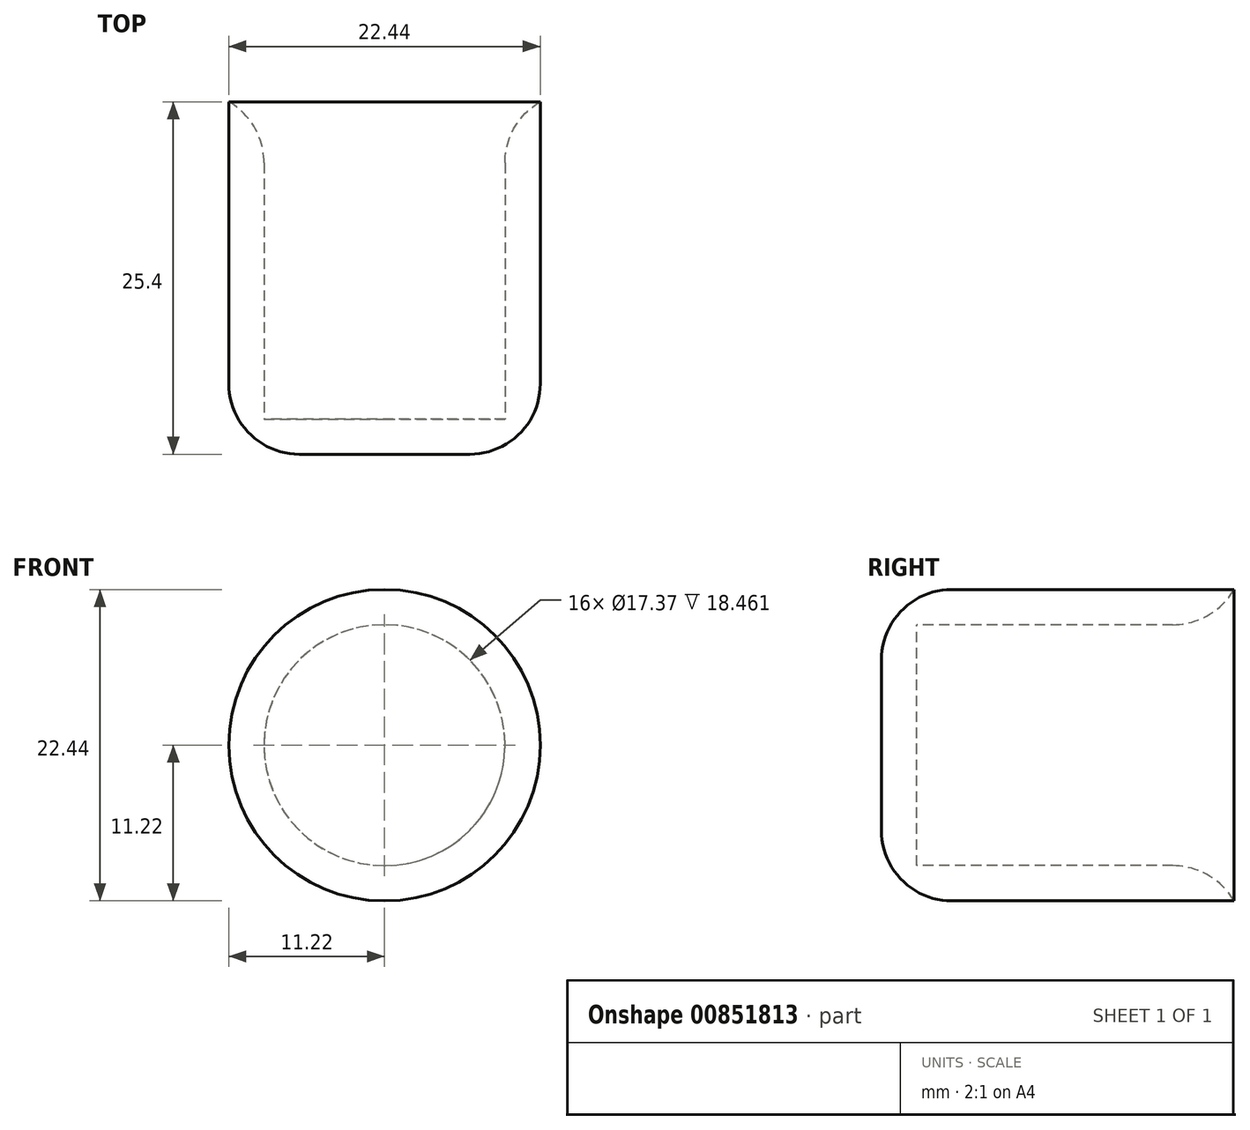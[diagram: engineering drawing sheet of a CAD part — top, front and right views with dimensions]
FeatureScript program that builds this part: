
annotation { "Feature Type Name" : "Feature", "Feature Type Description" : "" }
export const myFeature = defineFeature(function(context is Context, id is Id, definition is map)
    precondition{}
    {
        {
            var Q0;
            Q0=qCreatedBy(makeId("Top.planeOp"),FACE);
            var sketch = newSketch(context, id + "F0", { "sketchPlane" : qUnion([Q0])});
            skLineSegment(sketch, "E0.bottom", {"start": v(0, 0) * mm, "end": v(11.22, 0) * mm});
            skLineSegment(sketch, "E0.top", {"start": v(0, 25.4) * mm, "end": v(11.22, 25.4) * mm});
            skLineSegment(sketch, "E0.left", {"start": v(0, 0) * mm, "end": v(0, 25.4) * mm});
            skLineSegment(sketch, "E0.right", {"start": v(11.22, 0) * mm, "end": v(11.22, 25.4) * mm});
            skSolve(sketch);
        }
        {
            var Q0;
            Q0=makeQuery(id+"F0.imprint","IMPRINT",FACE,{"disambiguationData":[TD([[makeQuery(id+"F0.imprint","IMPRINT",EDGE,{"derivedFrom":sQuery(id+"F0.wireOp",EDGE,"E0.bottom")}),1.0]])]});
            var Q1;
            Q1=sQuery(id+"F0.wireOp",EDGE,"E0.left");
            revolve(context, id + "F1", {"surfaceOperationType" : NewSurfaceOperationType.NEW, "entities" : qUnion([Q0]), "axis" : qUnion([Q1]), "revolveType" : RevolveType.FULL});
        }
        {
            var Q0;
            Q0=makeQuery(id+"F1.opRevolve","SWEPT_FACE",FACE,{"disambiguationData":[OSD([sQuery(id+"F0.wireOp",EDGE,"E0.top")])]});
            shell(context, id + "F2", {"entities" : qUnion([Q0]), "thickness" : 2.54 * mm});
        }
        {
            var Q0;
            Q0=makeQuery(id+"F2.opShell","OFFSET_EDGE",EDGE,{"disambiguationData":[OSD([sQuery(id+"F0.wireOp",EDGE,"E0.top"),sQuery(id+"F0.wireOp",EDGE,"E0.right")])]});
            fillet(context, id + "F3", {"entities" : qUnion([Q0]), "radius" : 5.08 * mm, "tangentPropagation" : true, "allowEdgeOverflow" : false});
        }
        {
            var Q0;
            Q0=makeQuery(id+"F1.opRevolve","SWEPT_EDGE",EDGE,{"disambiguationData":[OSD([sQuery(id+"F0.wireOp",EDGE,"E0.bottom"),sQuery(id+"F0.wireOp",EDGE,"E0.right")])]});
            fillet(context, id + "F4", {"entities" : qUnion([Q0]), "radius" : 5.08 * mm, "tangentPropagation" : true, "allowEdgeOverflow" : false});
        }
    });
